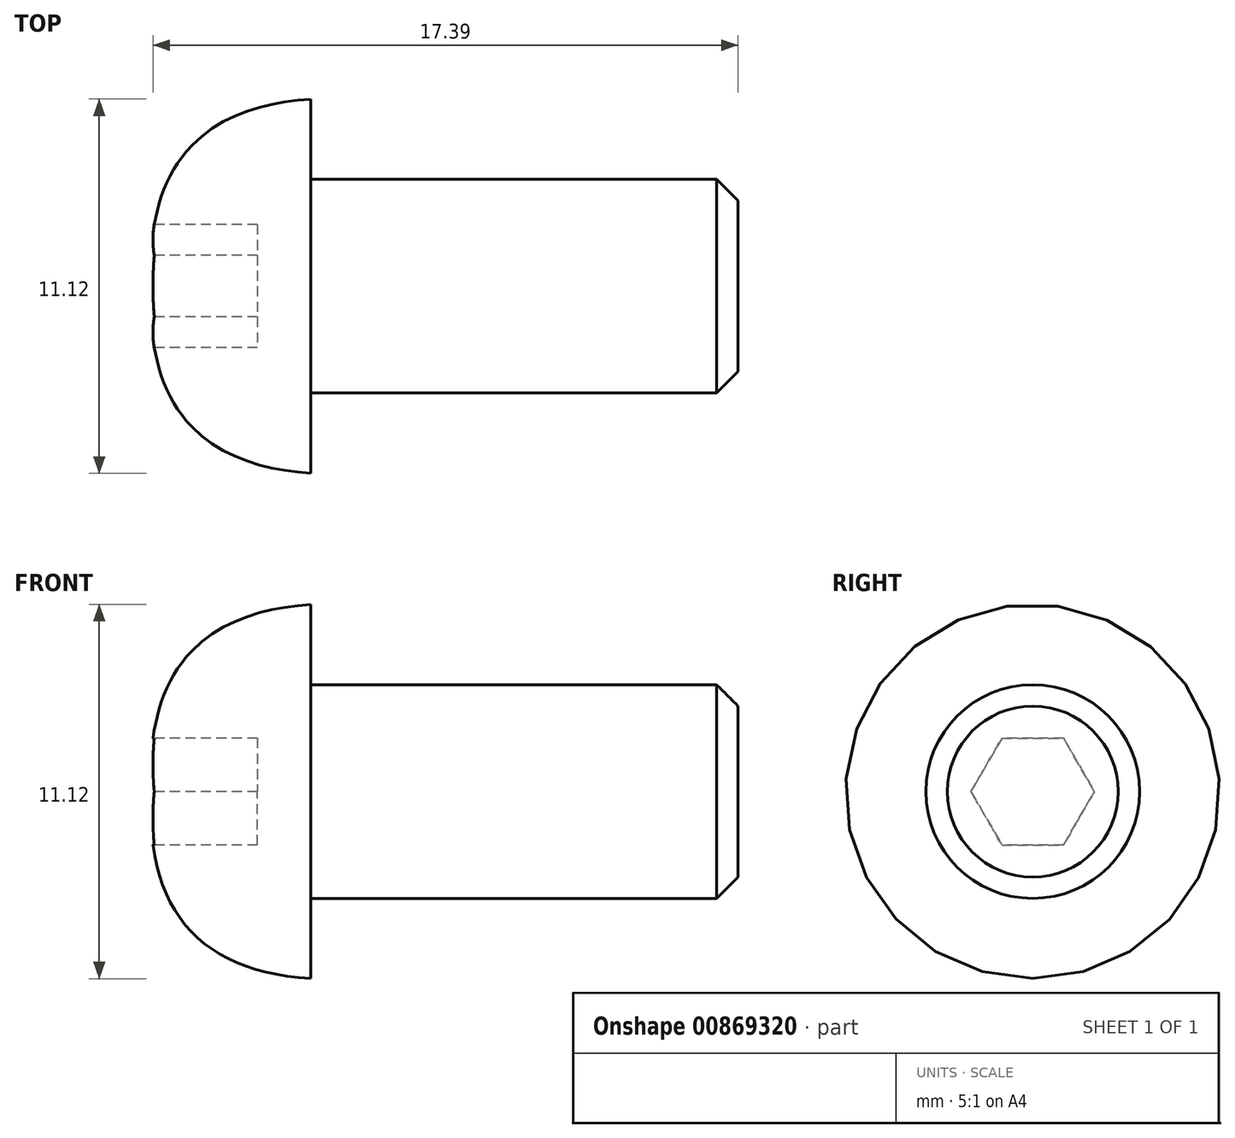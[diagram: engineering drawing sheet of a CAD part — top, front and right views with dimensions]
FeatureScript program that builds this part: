
annotation { "Feature Type Name" : "Feature", "Feature Type Description" : "" }
export const myFeature = defineFeature(function(context is Context, id is Id, definition is map)
    precondition{}
    {
        {
            var Q0;
            Q0=qCreatedBy(makeId("Front.planeOp"),FACE);
            var sketch = newSketch(context, id + "F0", { "sketchPlane" : qUnion([Q0])});
            skPoint(sketch, "E0.middle", {"position": v(0, 0) * mm});
            skLineSegment(sketch, "E1.bottom", {"start": v(-17.46, -5.56) * mm, "end": v(-12.7, -5.56) * mm});
            skLineSegment(sketch, "E1.top", {"start": v(-17.46, 5.56) * mm, "end": v(-12.7, 5.56) * mm});
            skLineSegment(sketch, "E1.left", {"start": v(-17.46, -5.56) * mm, "end": v(-17.46, 5.56) * mm});
            skLineSegment(sketch, "E2.bottom", {"start": v(-12.7, 3.17) * mm, "end": v(0, 3.18) * mm});
            skLineSegment(sketch, "E2.top", {"start": v(-12.7, -3.18) * mm, "end": v(0, -3.17) * mm});
            skLineSegment(sketch, "E2.right", {"start": v(0, 3.18) * mm, "end": v(0, -3.17) * mm});
            skLineSegment(sketch, "E3", {"start": v(-12.7, -5.56) * mm, "end": v(-12.7, 5.56) * mm});
            skLineSegment(sketch, "E4", {"start": v(0, 0) * mm, "end": v(-17.46, 0) * mm});
            skSolve(sketch);
        }
        {
            var Q0;
            {var subQ5=sQuery(id+"F0.wireOp",EDGE,"E1.top");Q0=makeQuery(id+"F0.imprint","IMPRINT",FACE,{"disambiguationData":[TD([[makeQuery(id+"F0.imprint","IMPRINT",EDGE,{"derivedFrom":subQ5}),-1.0]])]});}
            var Q1;
            Q1=sQuery(id+"F0.wireOp",EDGE,"E4");
            revolve(context, id + "F1", {"surfaceOperationType" : NewSurfaceOperationType.NEW, "entities" : qUnion([Q0]), "axis" : qUnion([Q1]), "revolveType" : RevolveType.FULL});
        }
        {
            var Q0;
            {var subQ0=sQuery(id+"F0.wireOp",EDGE,"E2.bottom");Q0=makeQuery(id+"F0.imprint","IMPRINT",FACE,{"disambiguationData":[TD([[makeQuery(id+"F0.imprint","IMPRINT",EDGE,{"derivedFrom":subQ0}),-1.0]])]});}
            var Q1;
            Q1=sQuery(id+"F0.wireOp",EDGE,"E4");
            revolve(context, id + "F2", {"operationType" : NewBodyOperationType.ADD, "surfaceOperationType" : NewSurfaceOperationType.NEW, "entities" : qUnion([Q0]), "axis" : qUnion([Q1]), "revolveType" : RevolveType.FULL});
        }
        {
            var Q0;
            Q0=makeQuery(id+"F1.opRevolve","SWEPT_FACE",FACE,{"disambiguationData":[OSD([sQuery(id+"F0.wireOp",EDGE,"E1.left")])]});
            var sketch = newSketch(context, id + "F3", { "sketchPlane" : qUnion([Q0])});
            skCircle(sketch, "E5.cCircle", {"center": v(0, 0) * mm, "radius": 1.59 * mm, "construction": true});
            skLineSegment(sketch, "E5.0", {"start": v(0.92, 1.59) * mm, "end": v(1.83, 0) * mm});
            skLineSegment(sketch, "E5.1", {"start": v(1.83, 0) * mm, "end": v(0.92, -1.59) * mm});
            skLineSegment(sketch, "E5.2", {"start": v(0.92, -1.59) * mm, "end": v(-0.92, -1.59) * mm});
            skLineSegment(sketch, "E5.3", {"start": v(-0.92, -1.59) * mm, "end": v(-1.83, 0) * mm});
            skLineSegment(sketch, "E5.4", {"start": v(-1.83, 0) * mm, "end": v(-0.92, 1.59) * mm});
            skLineSegment(sketch, "E5.5", {"start": v(-0.92, 1.59) * mm, "end": v(0.92, 1.59) * mm});
            skPoint(sketch, "E5.0.midPoint", {"position": v(1.37, 0.8) * mm});
            skSolve(sketch);
        }
        {
            var Q0;
            Q0=makeQuery(id+"F3.imprint","IMPRINT",FACE,{"disambiguationData":[TD([[makeQuery(id+"F3.imprint","IMPRINT",EDGE,{"derivedFrom":sQuery(id+"F3.wireOp",EDGE,"E5.0")}),-1.0]])]});
            extrude(context, id + "F4", {"entities" : qUnion([Q0]), "operationType" : NewBodyOperationType.REMOVE, "oppositeDirection" : true, "depth" : 3.17 * mm, "offsetDistance" : 25.4 * mm});
        }
        {
            var Q0;
            Q0=makeQuery(id+"F1.opRevolve","SWEPT_EDGE",EDGE,{"disambiguationData":[OSD([sQuery(id+"F0.wireOp",EDGE,"E1.top"),sQuery(id+"F0.wireOp",EDGE,"E1.left")])]});
            fillet(context, id + "F5", {"entities" : qUnion([Q0]), "radius" : 5.08 * mm, "tangentPropagation" : true, "rho" : .5, "crossSection" : FilletCrossSection.CONIC, "allowEdgeOverflow" : false});
        }
        {
            var Q0;
            Q0=makeQuery(id+"F2.opRevolve","SWEPT_EDGE",EDGE,{"disambiguationData":[OSD([sQuery(id+"F0.wireOp",EDGE,"E2.bottom"),sQuery(id+"F0.wireOp",EDGE,"E2.right")])]});
            chamfer(context, id + "F6", {"entities" : qUnion([Q0]), "width" : 0.64 * mm, "tangentPropagation" : true});
        }
    });
